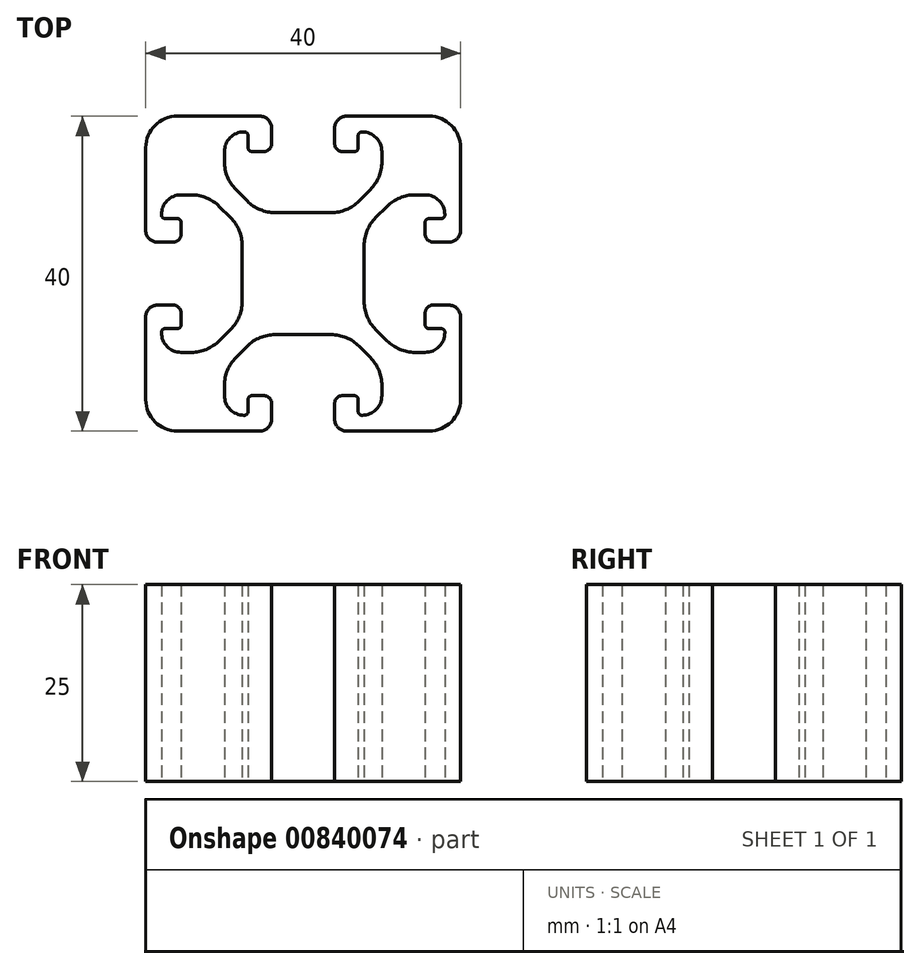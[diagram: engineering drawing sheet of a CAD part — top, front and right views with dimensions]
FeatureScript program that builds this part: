
annotation { "Feature Type Name" : "Feature", "Feature Type Description" : "" }
export const myFeature = defineFeature(function(context is Context, id is Id, definition is map)
    precondition{}
    {
        {
            var Q0;
            Q0=qCreatedBy(makeId("Top.planeOp"),FACE);
            var sketch = newSketch(context, id + "F0", { "sketchPlane" : qUnion([Q0])});
            skArc(sketch, "E0.0.0", {"start": v(-18.5, -4) * mm, "mid": v(-19.56, -4.44) * mm, "end": v(-20, -5.5) * mm});
            skLineSegment(sketch, "E0.0.1", {"start": v(-20, -5.5) * mm, "end": v(-20, -16) * mm});
            skArc(sketch, "E0.0.2", {"start": v(-20, -16) * mm, "mid": v(-18.83, -18.83) * mm, "end": v(-16, -20) * mm});
            skLineSegment(sketch, "E0.0.3", {"start": v(-16, -20) * mm, "end": v(-5.5, -20) * mm});
            skArc(sketch, "E0.0.4", {"start": v(-5.5, -20) * mm, "mid": v(-4.44, -19.56) * mm, "end": v(-4, -18.5) * mm});
            skLineSegment(sketch, "E0.0.5", {"start": v(-4, -18.5) * mm, "end": v(-4, -16.5) * mm});
            skArc(sketch, "E0.0.6", {"start": v(-4, -16.5) * mm, "mid": v(-4.3, -15.8) * mm, "end": v(-5, -15.5) * mm});
            skLineSegment(sketch, "E0.0.7", {"start": v(-5, -15.5) * mm, "end": v(-6.5, -15.5) * mm});
            skArc(sketch, "E0.0.8", {"start": v(-6.5, -15.5) * mm, "mid": v(-6.85, -15.65) * mm, "end": v(-7, -16) * mm});
            skLineSegment(sketch, "E0.0.9", {"start": v(-7, -16) * mm, "end": v(-7, -17.55) * mm});
            skArc(sketch, "E0.0.10", {"start": v(-7, -17.55) * mm, "mid": v(-7.13, -17.87) * mm, "end": v(-7.45, -18) * mm});
            skLineSegment(sketch, "E0.0.11", {"start": v(-7.45, -18) * mm, "end": v(-7.5, -18) * mm});
            skArc(sketch, "E0.0.12", {"start": v(-7.5, -18) * mm, "mid": v(-9.27, -17.27) * mm, "end": v(-10, -15.5) * mm});
            skLineSegment(sketch, "E0.0.13", {"start": v(-10, -15.5) * mm, "end": v(-10, -14.2) * mm});
            skArc(sketch, "E0.0.14", {"start": v(-10, -14.2) * mm, "mid": v(-9.62, -12.28) * mm, "end": v(-8.54, -10.66) * mm});
            skLineSegment(sketch, "E0.0.15", {"start": v(-8.54, -10.66) * mm, "end": v(-7.1, -9.21) * mm});
            skArc(sketch, "E0.0.16", {"start": v(-7.1, -9.21) * mm, "mid": v(-5.47, -8.13) * mm, "end": v(-3.56, -7.75) * mm});
            skLineSegment(sketch, "E0.0.17", {"start": v(-3.56, -7.75) * mm, "end": v(3.56, -7.75) * mm});
            skArc(sketch, "E0.0.18", {"start": v(3.56, -7.75) * mm, "mid": v(5.47, -8.13) * mm, "end": v(7.1, -9.21) * mm});
            skLineSegment(sketch, "E0.0.19", {"start": v(7.1, -9.21) * mm, "end": v(8.54, -10.66) * mm});
            skArc(sketch, "E0.0.20", {"start": v(8.54, -10.66) * mm, "mid": v(9.62, -12.28) * mm, "end": v(10, -14.2) * mm});
            skLineSegment(sketch, "E0.0.21", {"start": v(10, -14.2) * mm, "end": v(10, -15.5) * mm});
            skArc(sketch, "E0.0.22", {"start": v(10, -15.5) * mm, "mid": v(9.27, -17.27) * mm, "end": v(7.5, -18) * mm});
            skLineSegment(sketch, "E0.0.23", {"start": v(7.5, -18) * mm, "end": v(7.45, -18) * mm});
            skArc(sketch, "E0.0.24", {"start": v(7.45, -18) * mm, "mid": v(7.13, -17.87) * mm, "end": v(7, -17.55) * mm});
            skLineSegment(sketch, "E0.0.25", {"start": v(7, -17.55) * mm, "end": v(7, -16) * mm});
            skArc(sketch, "E0.0.26", {"start": v(7, -16) * mm, "mid": v(6.85, -15.65) * mm, "end": v(6.5, -15.5) * mm});
            skLineSegment(sketch, "E0.0.27", {"start": v(6.5, -15.5) * mm, "end": v(5, -15.5) * mm});
            skArc(sketch, "E0.0.28", {"start": v(5, -15.5) * mm, "mid": v(4.3, -15.8) * mm, "end": v(4, -16.5) * mm});
            skLineSegment(sketch, "E0.0.29", {"start": v(4, -16.5) * mm, "end": v(4, -18.5) * mm});
            skArc(sketch, "E0.0.30", {"start": v(4, -18.5) * mm, "mid": v(4.44, -19.56) * mm, "end": v(5.5, -20) * mm});
            skLineSegment(sketch, "E0.0.31", {"start": v(5.5, -20) * mm, "end": v(16, -20) * mm});
            skArc(sketch, "E0.0.32", {"start": v(16, -20) * mm, "mid": v(18.83, -18.83) * mm, "end": v(20, -16) * mm});
            skLineSegment(sketch, "E0.0.33", {"start": v(20, -16) * mm, "end": v(20, -5.5) * mm});
            skArc(sketch, "E0.0.34", {"start": v(20, -5.5) * mm, "mid": v(19.56, -4.44) * mm, "end": v(18.5, -4) * mm});
            skLineSegment(sketch, "E0.0.35", {"start": v(18.5, -4) * mm, "end": v(16.5, -4) * mm});
            skArc(sketch, "E0.0.36", {"start": v(16.5, -4) * mm, "mid": v(15.8, -4.3) * mm, "end": v(15.5, -5) * mm});
            skLineSegment(sketch, "E0.0.37", {"start": v(15.5, -5) * mm, "end": v(15.5, -6.5) * mm});
            skArc(sketch, "E0.0.38", {"start": v(15.5, -6.5) * mm, "mid": v(15.65, -6.85) * mm, "end": v(16, -7) * mm});
            skLineSegment(sketch, "E0.0.39", {"start": v(16, -7) * mm, "end": v(17.55, -7) * mm});
            skArc(sketch, "E0.0.40", {"start": v(17.55, -7) * mm, "mid": v(17.87, -7.13) * mm, "end": v(18, -7.45) * mm});
            skLineSegment(sketch, "E0.0.41", {"start": v(18, -7.45) * mm, "end": v(18, -7.5) * mm});
            skArc(sketch, "E0.0.42", {"start": v(18, -7.5) * mm, "mid": v(17.27, -9.27) * mm, "end": v(15.5, -10) * mm});
            skLineSegment(sketch, "E0.0.43", {"start": v(15.5, -10) * mm, "end": v(14.2, -10) * mm});
            skArc(sketch, "E0.0.44", {"start": v(14.2, -10) * mm, "mid": v(12.28, -9.62) * mm, "end": v(10.66, -8.54) * mm});
            skLineSegment(sketch, "E0.0.45", {"start": v(10.66, -8.54) * mm, "end": v(9.21, -7.1) * mm});
            skArc(sketch, "E0.0.46", {"start": v(9.21, -7.1) * mm, "mid": v(8.13, -5.47) * mm, "end": v(7.75, -3.56) * mm});
            skLineSegment(sketch, "E0.0.47", {"start": v(7.75, -3.56) * mm, "end": v(7.75, 3.56) * mm});
            skArc(sketch, "E0.0.48", {"start": v(7.75, 3.56) * mm, "mid": v(8.13, 5.47) * mm, "end": v(9.21, 7.1) * mm});
            skLineSegment(sketch, "E0.0.49", {"start": v(9.21, 7.1) * mm, "end": v(10.66, 8.54) * mm});
            skArc(sketch, "E0.0.50", {"start": v(10.66, 8.54) * mm, "mid": v(12.28, 9.62) * mm, "end": v(14.2, 10) * mm});
            skLineSegment(sketch, "E0.0.51", {"start": v(14.2, 10) * mm, "end": v(15.5, 10) * mm});
            skArc(sketch, "E0.0.52", {"start": v(15.5, 10) * mm, "mid": v(17.27, 9.27) * mm, "end": v(18, 7.5) * mm});
            skLineSegment(sketch, "E0.0.53", {"start": v(18, 7.5) * mm, "end": v(18, 7.45) * mm});
            skArc(sketch, "E0.0.54", {"start": v(18, 7.45) * mm, "mid": v(17.87, 7.13) * mm, "end": v(17.55, 7) * mm});
            skLineSegment(sketch, "E0.0.55", {"start": v(17.55, 7) * mm, "end": v(16, 7) * mm});
            skArc(sketch, "E0.0.56", {"start": v(16, 7) * mm, "mid": v(15.65, 6.85) * mm, "end": v(15.5, 6.5) * mm});
            skLineSegment(sketch, "E0.0.57", {"start": v(15.5, 6.5) * mm, "end": v(15.5, 5) * mm});
            skArc(sketch, "E0.0.58", {"start": v(15.5, 5) * mm, "mid": v(15.8, 4.3) * mm, "end": v(16.5, 4) * mm});
            skLineSegment(sketch, "E0.0.59", {"start": v(16.5, 4) * mm, "end": v(18.5, 4) * mm});
            skArc(sketch, "E0.0.60", {"start": v(18.5, 4) * mm, "mid": v(19.56, 4.44) * mm, "end": v(20, 5.5) * mm});
            skLineSegment(sketch, "E0.0.61", {"start": v(20, 5.5) * mm, "end": v(20, 16) * mm});
            skArc(sketch, "E0.0.62", {"start": v(20, 16) * mm, "mid": v(18.83, 18.83) * mm, "end": v(16, 20) * mm});
            skLineSegment(sketch, "E0.0.63", {"start": v(16, 20) * mm, "end": v(5.5, 20) * mm});
            skArc(sketch, "E0.0.64", {"start": v(5.5, 20) * mm, "mid": v(4.44, 19.56) * mm, "end": v(4, 18.5) * mm});
            skLineSegment(sketch, "E0.0.65", {"start": v(4, 18.5) * mm, "end": v(4, 16.5) * mm});
            skArc(sketch, "E0.0.66", {"start": v(4, 16.5) * mm, "mid": v(4.3, 15.8) * mm, "end": v(5, 15.5) * mm});
            skLineSegment(sketch, "E0.0.67", {"start": v(5, 15.5) * mm, "end": v(6.5, 15.5) * mm});
            skArc(sketch, "E0.0.68", {"start": v(6.5, 15.5) * mm, "mid": v(6.85, 15.65) * mm, "end": v(7, 16) * mm});
            skLineSegment(sketch, "E0.0.69", {"start": v(7, 16) * mm, "end": v(7, 17.55) * mm});
            skArc(sketch, "E0.0.70", {"start": v(7, 17.55) * mm, "mid": v(7.13, 17.87) * mm, "end": v(7.45, 18) * mm});
            skLineSegment(sketch, "E0.0.71", {"start": v(7.45, 18) * mm, "end": v(7.5, 18) * mm});
            skArc(sketch, "E0.0.72", {"start": v(7.5, 18) * mm, "mid": v(9.27, 17.27) * mm, "end": v(10, 15.5) * mm});
            skLineSegment(sketch, "E0.0.73", {"start": v(10, 15.5) * mm, "end": v(10, 14.2) * mm});
            skArc(sketch, "E0.0.74", {"start": v(10, 14.2) * mm, "mid": v(9.62, 12.28) * mm, "end": v(8.54, 10.66) * mm});
            skLineSegment(sketch, "E0.0.75", {"start": v(8.54, 10.66) * mm, "end": v(7.1, 9.21) * mm});
            skArc(sketch, "E0.0.76", {"start": v(7.1, 9.21) * mm, "mid": v(5.47, 8.13) * mm, "end": v(3.56, 7.75) * mm});
            skLineSegment(sketch, "E0.0.77", {"start": v(3.56, 7.75) * mm, "end": v(-3.56, 7.75) * mm});
            skArc(sketch, "E0.0.78", {"start": v(-3.56, 7.75) * mm, "mid": v(-5.47, 8.13) * mm, "end": v(-7.1, 9.21) * mm});
            skLineSegment(sketch, "E0.0.79", {"start": v(-7.1, 9.21) * mm, "end": v(-8.54, 10.66) * mm});
            skArc(sketch, "E0.0.80", {"start": v(-8.54, 10.66) * mm, "mid": v(-9.62, 12.28) * mm, "end": v(-10, 14.2) * mm});
            skLineSegment(sketch, "E0.0.81", {"start": v(-10, 14.2) * mm, "end": v(-10, 15.5) * mm});
            skArc(sketch, "E0.0.82", {"start": v(-10, 15.5) * mm, "mid": v(-9.27, 17.27) * mm, "end": v(-7.5, 18) * mm});
            skLineSegment(sketch, "E0.0.83", {"start": v(-7.5, 18) * mm, "end": v(-7.45, 18) * mm});
            skArc(sketch, "E0.0.84", {"start": v(-7.45, 18) * mm, "mid": v(-7.13, 17.87) * mm, "end": v(-7, 17.55) * mm});
            skLineSegment(sketch, "E0.0.85", {"start": v(-7, 17.55) * mm, "end": v(-7, 16) * mm});
            skArc(sketch, "E0.0.86", {"start": v(-7, 16) * mm, "mid": v(-6.85, 15.65) * mm, "end": v(-6.5, 15.5) * mm});
            skLineSegment(sketch, "E0.0.87", {"start": v(-6.5, 15.5) * mm, "end": v(-5, 15.5) * mm});
            skArc(sketch, "E0.0.88", {"start": v(-5, 15.5) * mm, "mid": v(-4.3, 15.8) * mm, "end": v(-4, 16.5) * mm});
            skLineSegment(sketch, "E0.0.89", {"start": v(-4, 16.5) * mm, "end": v(-4, 18.5) * mm});
            skArc(sketch, "E0.0.90", {"start": v(-4, 18.5) * mm, "mid": v(-4.44, 19.56) * mm, "end": v(-5.5, 20) * mm});
            skLineSegment(sketch, "E0.0.91", {"start": v(-5.5, 20) * mm, "end": v(-16, 20) * mm});
            skArc(sketch, "E0.0.92", {"start": v(-16, 20) * mm, "mid": v(-18.83, 18.83) * mm, "end": v(-20, 16) * mm});
            skLineSegment(sketch, "E0.0.93", {"start": v(-20, 16) * mm, "end": v(-20, 5.5) * mm});
            skArc(sketch, "E0.0.94", {"start": v(-20, 5.5) * mm, "mid": v(-19.56, 4.44) * mm, "end": v(-18.5, 4) * mm});
            skLineSegment(sketch, "E0.0.95", {"start": v(-18.5, 4) * mm, "end": v(-16.5, 4) * mm});
            skArc(sketch, "E0.0.96", {"start": v(-16.5, 4) * mm, "mid": v(-15.8, 4.3) * mm, "end": v(-15.5, 5) * mm});
            skLineSegment(sketch, "E0.0.97", {"start": v(-15.5, 5) * mm, "end": v(-15.5, 6.5) * mm});
            skArc(sketch, "E0.0.98", {"start": v(-15.5, 6.5) * mm, "mid": v(-15.65, 6.85) * mm, "end": v(-16, 7) * mm});
            skLineSegment(sketch, "E0.0.99", {"start": v(-16, 7) * mm, "end": v(-17.55, 7) * mm});
            skArc(sketch, "E0.0.100", {"start": v(-17.55, 7) * mm, "mid": v(-17.87, 7.13) * mm, "end": v(-18, 7.45) * mm});
            skLineSegment(sketch, "E0.0.101", {"start": v(-18, 7.45) * mm, "end": v(-18, 7.5) * mm});
            skArc(sketch, "E0.0.102", {"start": v(-18, 7.5) * mm, "mid": v(-17.27, 9.27) * mm, "end": v(-15.5, 10) * mm});
            skLineSegment(sketch, "E0.0.103", {"start": v(-15.5, 10) * mm, "end": v(-14.2, 10) * mm});
            skArc(sketch, "E0.0.104", {"start": v(-14.2, 10) * mm, "mid": v(-12.28, 9.62) * mm, "end": v(-10.66, 8.54) * mm});
            skLineSegment(sketch, "E0.0.105", {"start": v(-10.66, 8.54) * mm, "end": v(-9.21, 7.1) * mm});
            skArc(sketch, "E0.0.106", {"start": v(-9.21, 7.1) * mm, "mid": v(-8.13, 5.47) * mm, "end": v(-7.75, 3.56) * mm});
            skLineSegment(sketch, "E0.0.107", {"start": v(-7.75, 3.56) * mm, "end": v(-7.75, -3.56) * mm});
            skArc(sketch, "E0.0.108", {"start": v(-7.75, -3.56) * mm, "mid": v(-8.13, -5.47) * mm, "end": v(-9.21, -7.1) * mm});
            skLineSegment(sketch, "E0.0.109", {"start": v(-9.21, -7.1) * mm, "end": v(-10.66, -8.54) * mm});
            skArc(sketch, "E0.0.110", {"start": v(-10.66, -8.54) * mm, "mid": v(-12.28, -9.62) * mm, "end": v(-14.2, -10) * mm});
            skLineSegment(sketch, "E0.0.111", {"start": v(-14.2, -10) * mm, "end": v(-15.5, -10) * mm});
            skArc(sketch, "E0.0.112", {"start": v(-15.5, -10) * mm, "mid": v(-17.27, -9.27) * mm, "end": v(-18, -7.5) * mm});
            skLineSegment(sketch, "E0.0.113", {"start": v(-18, -7.5) * mm, "end": v(-18, -7.45) * mm});
            skArc(sketch, "E0.0.114", {"start": v(-18, -7.45) * mm, "mid": v(-17.87, -7.13) * mm, "end": v(-17.55, -7) * mm});
            skLineSegment(sketch, "E0.0.115", {"start": v(-17.55, -7) * mm, "end": v(-16, -7) * mm});
            skArc(sketch, "E0.0.116", {"start": v(-16, -7) * mm, "mid": v(-15.65, -6.85) * mm, "end": v(-15.5, -6.5) * mm});
            skLineSegment(sketch, "E0.0.117", {"start": v(-15.5, -6.5) * mm, "end": v(-15.5, -5) * mm});
            skArc(sketch, "E0.0.118", {"start": v(-15.5, -5) * mm, "mid": v(-15.8, -4.3) * mm, "end": v(-16.5, -4) * mm});
            skLineSegment(sketch, "E0.0.119", {"start": v(-16.5, -4) * mm, "end": v(-18.5, -4) * mm});
            skSolve(sketch);
        }
        {
            var Q0;
            Q0=makeQuery(id+"F0.imprint","IMPRINT",FACE,{"disambiguationData":[TD([[makeQuery(id+"F0.imprint","IMPRINT",EDGE,{"derivedFrom":sQuery(id+"F0.wireOp",EDGE,"E0.0.0")}),1.0]])]});
            extrude(context, id + "F1", {"entities" : qUnion([Q0]), "depth" : 25 * mm, "offsetDistance" : 25 * mm});
        }
    });
